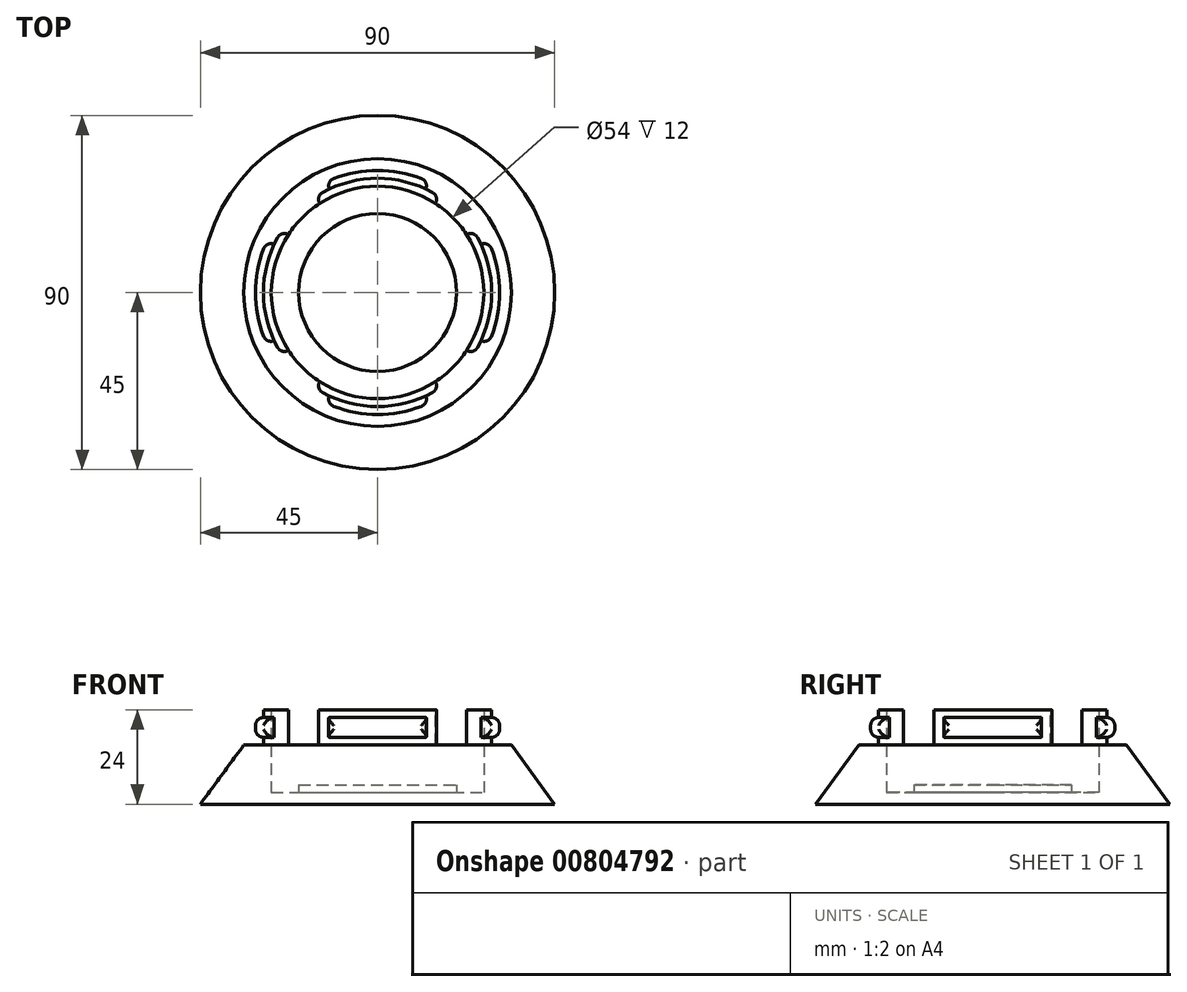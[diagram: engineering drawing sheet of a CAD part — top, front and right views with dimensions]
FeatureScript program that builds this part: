
annotation { "Feature Type Name" : "Feature", "Feature Type Description" : "" }
export const myFeature = defineFeature(function(context is Context, id is Id, definition is map)
    precondition{}
    {
        {
            var Q0;
            Q0=qCreatedBy(makeId("Front.planeOp"),FACE);
            var sketch = newSketch(context, id + "F0", { "sketchPlane" : qUnion([Q0])});
            skLineSegment(sketch, "E0", {"start": v(-45, 0) * mm, "end": v(0, 0) * mm});
            skLineSegment(sketch, "E1", {"start": v(0, 0) * mm, "end": v(0, 3) * mm});
            skLineSegment(sketch, "E2", {"start": v(-27, 3) * mm, "end": v(-27, 15) * mm});
            skLineSegment(sketch, "E3", {"start": v(-27, 15) * mm, "end": v(-34, 15) * mm});
            skLineSegment(sketch, "E4", {"start": v(-34, 15) * mm, "end": v(-45, 0) * mm});
            skLineSegment(sketch, "E5", {"start": v(-20.05, 3) * mm, "end": v(-20.05, 4.95) * mm});
            skLineSegment(sketch, "E6", {"start": v(-20.05, 4.95) * mm, "end": v(0, 4.95) * mm});
            skLineSegment(sketch, "E7", {"start": v(0, 4.95) * mm, "end": v(0, 3) * mm});
            skLineSegment(sketch, "E8", {"start": v(-27, 3) * mm, "end": v(-20.05, 3) * mm});
            skSolve(sketch);
        }
        {
            var Q0;
            Q0=makeQuery(id+"F0.imprint","IMPRINT",FACE,{"disambiguationData":[TD([[makeQuery(id+"F0.imprint","IMPRINT",EDGE,{"derivedFrom":sQuery(id+"F0.wireOp",EDGE,"E0")}),1.0]])]});
            var Q1;
            Q1=sQuery(id+"F0.wireOp",EDGE,"E1");
            revolve(context, id + "F1", {"surfaceOperationType" : NewSurfaceOperationType.NEW, "entities" : qUnion([Q0]), "axis" : qUnion([Q1]), "revolveType" : RevolveType.FULL});
        }
        {
            var Q0;
            Q0=qCreatedBy(makeId("Front.planeOp"),FACE);
            var sketch = newSketch(context, id + "F2", { "sketchPlane" : qUnion([Q0])});
            skLineSegment(sketch, "E9", {"start": v(-27, 15) * mm, "end": v(-27, 24) * mm});
            skLineSegment(sketch, "E10", {"start": v(-27, 24) * mm, "end": v(-29, 24) * mm});
            skLineSegment(sketch, "E11", {"start": v(-29, 24) * mm, "end": v(-29, 15) * mm});
            skLineSegment(sketch, "E12", {"start": v(-29, 15) * mm, "end": v(-27, 15) * mm});
            skSolve(sketch);
        }
        {
            var Q0;
            Q0=makeQuery(id+"F2.imprint","IMPRINT",FACE,{"disambiguationData":[TD([[makeQuery(id+"F2.imprint","IMPRINT",EDGE,{"derivedFrom":sQuery(id+"F2.wireOp",EDGE,"E9")}),1.0]])]});
            var Q1;
            Q1=sQuery(id+"F0.wireOp",EDGE,"E1");
            revolve(context, id + "F3", {"surfaceOperationType" : NewSurfaceOperationType.NEW, "entities" : qUnion([Q0]), "axis" : qUnion([Q1]), "revolveType" : RevolveType.SYMMETRIC, "angle" : 66 * degree});
        }
        {
            var Q0;
            Q0=makeQuery(id+"F3.opRevolve","CAP_EDGE",EDGE,{"disambiguationData":[OSD([sQuery(id+"F2.wireOp",EDGE,"E11")])],"isStart":false});
            fillet(context, id + "F4", {"entities" : qUnion([Q0]), "radius" : 2 * mm, "tangentPropagation" : true, "allowEdgeOverflow" : false});
        }
        {
            var Q0;
            Q0=makeQuery(id+"F3.opRevolve","CAP_EDGE",EDGE,{"disambiguationData":[OSD([sQuery(id+"F2.wireOp",EDGE,"E11")])],"isStart":true});
            fillet(context, id + "F5", {"entities" : qUnion([Q0]), "radius" : 2 * mm, "tangentPropagation" : true, "allowEdgeOverflow" : false});
        }
        {
            var Q0;
            Q0=qCreatedBy(makeId("Front.planeOp"),FACE);
            var sketch = newSketch(context, id + "F6", { "sketchPlane" : qUnion([Q0])});
            skLineSegment(sketch, "E13", {"start": v(-29, 22) * mm, "end": v(-31, 22) * mm});
            skLineSegment(sketch, "E14", {"start": v(-31, 22) * mm, "end": v(-31, 17) * mm});
            skLineSegment(sketch, "E15", {"start": v(-31, 17) * mm, "end": v(-29, 17) * mm});
            skLineSegment(sketch, "E16", {"start": v(-29, 17) * mm, "end": v(-29, 22) * mm});
            skSolve(sketch);
        }
        {
            var Q0;
            Q0 = qSketchRegion(id + "F6", true);
            var Q1;
            Q1=sQuery(id+"F0.wireOp",EDGE,"E1");
            revolve(context, id + "F7", {"operationType" : NewBodyOperationType.ADD, "surfaceOperationType" : NewSurfaceOperationType.NEW, "entities" : qUnion([Q0]), "axis" : qUnion([Q1]), "revolveType" : RevolveType.SYMMETRIC, "angle" : 50 * degree});
        }
        {
            var Q0;
            Q0=makeQuery(id+"F7.opRevolve","CAP_EDGE",EDGE,{"disambiguationData":[OSD([sQuery(id+"F6.wireOp",EDGE,"E14")])],"isStart":false});
            var Q1;
            Q1=makeQuery(id+"F7.opRevolve","CAP_EDGE",EDGE,{"disambiguationData":[OSD([sQuery(id+"F6.wireOp",EDGE,"E14")])],"isStart":true});
            var Q2;
            Q2=makeQuery(id+"F7.opRevolve","SWEPT_EDGE",EDGE,{"disambiguationData":[OSD([sQuery(id+"F6.wireOp",EDGE,"E13"),sQuery(id+"F6.wireOp",EDGE,"E14")])]});
            var Q3;
            Q3=makeQuery(id+"F7.opRevolve","SWEPT_EDGE",EDGE,{"disambiguationData":[OSD([sQuery(id+"F6.wireOp",EDGE,"E14"),sQuery(id+"F6.wireOp",EDGE,"E15")])]});
            fillet(context, id + "F8", {"entities" : qUnion([Q0, Q1, Q2, Q3]), "radius" : 2 * mm, "tangentPropagation" : true, "allowEdgeOverflow" : false});
        }
        {
            var Q0;
            Q0=makeQuery(id+"F3.opRevolve","SWEPT_BODY",BODY,{"disambiguationData":[OSD([sQuery(id+"F2.wireOp",EDGE,"E9"),sQuery(id+"F2.wireOp",EDGE,"E10"),sQuery(id+"F2.wireOp",EDGE,"E11"),sQuery(id+"F2.wireOp",EDGE,"E12")])]});
            var Q1;
            Q1=sQuery(id+"F0.wireOp",EDGE,"E1");
            circularPattern(context, id + "F9", {"entities" : qUnion([Q0]), "axis" : qUnion([Q1]), "angle" : 360 * degree, "instanceCount" : 4, "equalSpace" : true});
        }
    });
